# Revit family: IS_Ceratherm100New_A5833_BIM_DE
name_source: partatom
category: Plumbing Fixtures
revit_build: Autodesk Revit MEP 2016 (Build: 20161004_0715(x64)
units: mm (PartAtom-declared; Revit-internal decimal feet)

## family parameters
Always vertical = No
Cut with Voids When Loaded = No
OmniClass Number = 23.45.55.17
OmniClass Title = Mixing Faucets
Part Type = Normal
Room Calculation Point = No
Round Connector Dimension = Use Diameter
Shared = No
Work Plane-Based = No

## types (1)
- A5833AA - ICUBE COL.DOCCIA CERATHERM 100 NEW
    Accessories = www.idealstandard.de\ersatzteile
    AreaUnits = millimeters
    Assembly Code = C1030200
    AssetType = Fixed
    BIMObjectName = ISI_IdealStandard_MixerTaps_CERATHERM 100 NEW_A5833AA
    BIMobject category = Showers
    BOSUseNativeGeometries = 1
    BarCode = 4015413327732
    Brand url = http://www.idealstandard.co.uk
    CodePerformance = DIN 4109, Gruppe 1
    Color = Chrome
    ConnectionType = Plumbing
    Cost = 0 $
    CurrencyUnit = €
    Date of publishing = 6/23/2017
    Description = CERATHERM 100 NEW - Colonna doccia con termostatico esterno Ceratherm 100. Colonna doccia con fissaggio a muro estensibile sino a 30 mm. Supporto doccetta con scorrimento a pressione. Doccetta di dimensione 100x100 mm con riduttore di portata a 8 l/min. Soffione sottile di dimensione 200x200 mm con riduttore di portata a 12 l/min. Asta murale da 1051 mm con diametro 25 mm. Tubo flessibile Idealflex, in materiale plastico ad effetto metallico, da 1750 mm. Termostatico esterno doccia con uscita dell’acqua sia inferiore che superiore. Tecnologia Cool Body che garantisce protezione da eventuali scottature. Raccordi ad S da 1/2” regolabili per interasse da 137 mm a 163 mm. Blocco della temperatura a 40°. Tasto EKO per riduzione della portata dell’acqua fino al 50%. Deviatore integrato nella maniglia della portata.
    DurationUnit = year
    EAN code = https://4015413327732
    Edition number = 1
    ExpectedLife = 25
    Features = CERATHERM100 dual with IDEALRAIN CUBE rainshower M kit
    Finish = Chrome
    GrossWeight = 6,8 kg
    IFC Classification = Sanitary Terminal
    Installation instructions = http://www.idealstandard.de
    InstallationDate = 1900-12-31T23:59:59
    InstallationInstructions = www.idealstandard.de\produkte
    LinearUnits = millimeters
    Manufacturer name = Ideal Standard
    ManufacturerURL = www.idealstandard.de
    Material = Brass
    Material main = Brass
    Model = A5833AA
    ModelNumber = A5833AA
    ModelReference = IS Duschsystem M, IDEALRAIN CUBE m.Ceratherm 100 Brausetherm. AP, Chrom
    NBS Reference Code = 35-06-80
    NBS Reference Description = Shower Fittings Packages
    Name = ISI_IdealStandard_MixerTaps_CERATHERM 100 NEW_A5833AA
    Nominal height = 0
    Nominal width = 0
    NominalDepth = 0 mm  [stored 0 ft]
    NominalLength = 492 mm
    OmniClass Code = 23-31 17 00
    OmniClass Description = Showers
    Product Guid = 89c7f32f-ac5a-49ca-b4d7-75acd126109a
    Product SKU = A5833
    Product data url = https://bimobject.com
    Product family = CERATHERM 100 NEW
    Product group = Shower
    Product url = http://www.idealstandard.de
    ProductInformation = www.idealstandard.de
    QR code = http://bimobject.com
    Shape = Sculptured
    Size = 1182 x 340 x 492 mm
    Space = Internal
    Technical description = http://www.idealstandard.de
    URL = www.idealstandard.de
    Uniclass 1.4 Code = L7214
    Uniclass 1.4 Description = Showers
    Uniclass 2.0 Code = PR-35-06-80
    Uniclass 2.0 Description = Shower Fittings Packages
    Uniclass 2015 Code = Pr_40_20_87_75
    Uniclass 2015 Name = Shower fittings package
    Uniclass2015Code = Pr_40_20_87_98
    Uniclass2015Title = Washbasin taps
    Uniclass2015Version = Products v1.1
    Version = 1
    VolumeUnits = Litres
    Weight Net (Kg) = 6.8

note: [stored X ft] marks values corroborated as IEEE doubles in the binary element streams (Revit-internal decimal feet)

## geometry (parser evidence)
native form markers: Blend x2, Sweep x3
no freeform markers — native parametric forms only
